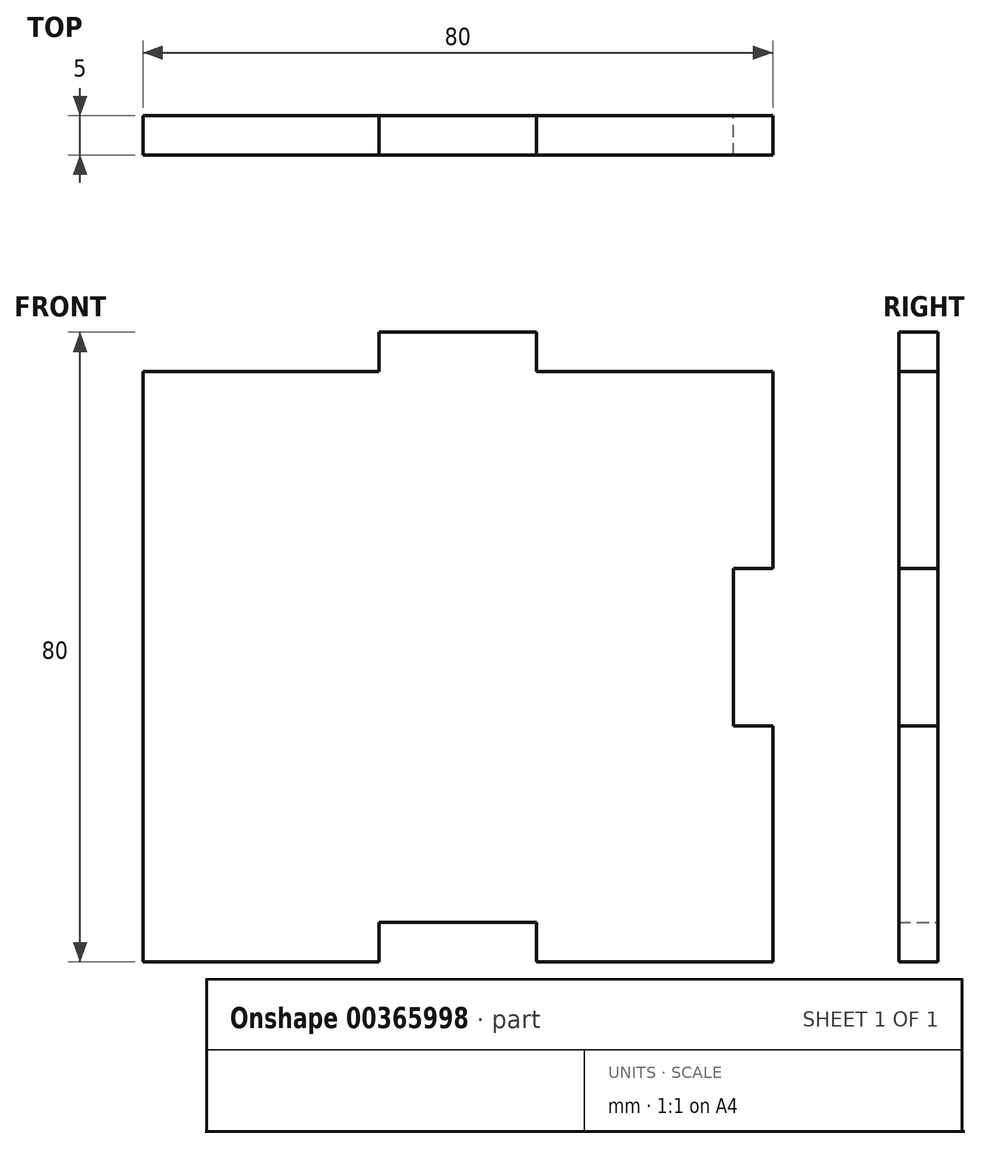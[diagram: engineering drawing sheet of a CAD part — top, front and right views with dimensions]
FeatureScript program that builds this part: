
annotation { "Feature Type Name" : "Feature", "Feature Type Description" : "" }
export const myFeature = defineFeature(function(context is Context, id is Id, definition is map)
    precondition{}
    {
        {
            var Q0;
            Q0=qCreatedBy(makeId("Front.planeOp"),FACE);
            var sketch = newSketch(context, id + "F0", { "sketchPlane" : qUnion([Q0])});
            skLineSegment(sketch, "E0", {"start": v(0, 0) * mm, "end": v(30, 0) * mm});
            skLineSegment(sketch, "E1", {"start": v(30, 0) * mm, "end": v(30, 5) * mm});
            skLineSegment(sketch, "E2", {"start": v(30, 5) * mm, "end": v(50, 5) * mm});
            skLineSegment(sketch, "E3", {"start": v(50, 5) * mm, "end": v(50, 0) * mm});
            skLineSegment(sketch, "E4", {"start": v(50, 0) * mm, "end": v(80, 0) * mm});
            skLineSegment(sketch, "E5", {"start": v(80, 0) * mm, "end": v(80, 30) * mm});
            skLineSegment(sketch, "E6", {"start": v(80, 30) * mm, "end": v(75, 30) * mm});
            skLineSegment(sketch, "E7", {"start": v(75, 30) * mm, "end": v(75, 50) * mm});
            skLineSegment(sketch, "E8", {"start": v(75, 50) * mm, "end": v(80, 50) * mm});
            skLineSegment(sketch, "E9", {"start": v(80, 50) * mm, "end": v(80, 75) * mm});
            skLineSegment(sketch, "E10", {"start": v(80, 75) * mm, "end": v(50, 75) * mm});
            skLineSegment(sketch, "E11", {"start": v(50, 75) * mm, "end": v(50, 80) * mm});
            skLineSegment(sketch, "E12", {"start": v(50, 80) * mm, "end": v(30, 80) * mm});
            skLineSegment(sketch, "E13", {"start": v(30, 80) * mm, "end": v(30, 75) * mm});
            skLineSegment(sketch, "E14", {"start": v(30, 75) * mm, "end": v(0, 75) * mm});
            skLineSegment(sketch, "E15", {"start": v(0, 75) * mm, "end": v(0, 0) * mm});
            skSolve(sketch);
        }
        {
            var Q0;
            Q0 = qSketchRegion(id + "F0", true);
            extrude(context, id + "F1", {"entities" : qUnion([Q0]), "depth" : 5 * mm});
        }
    });
